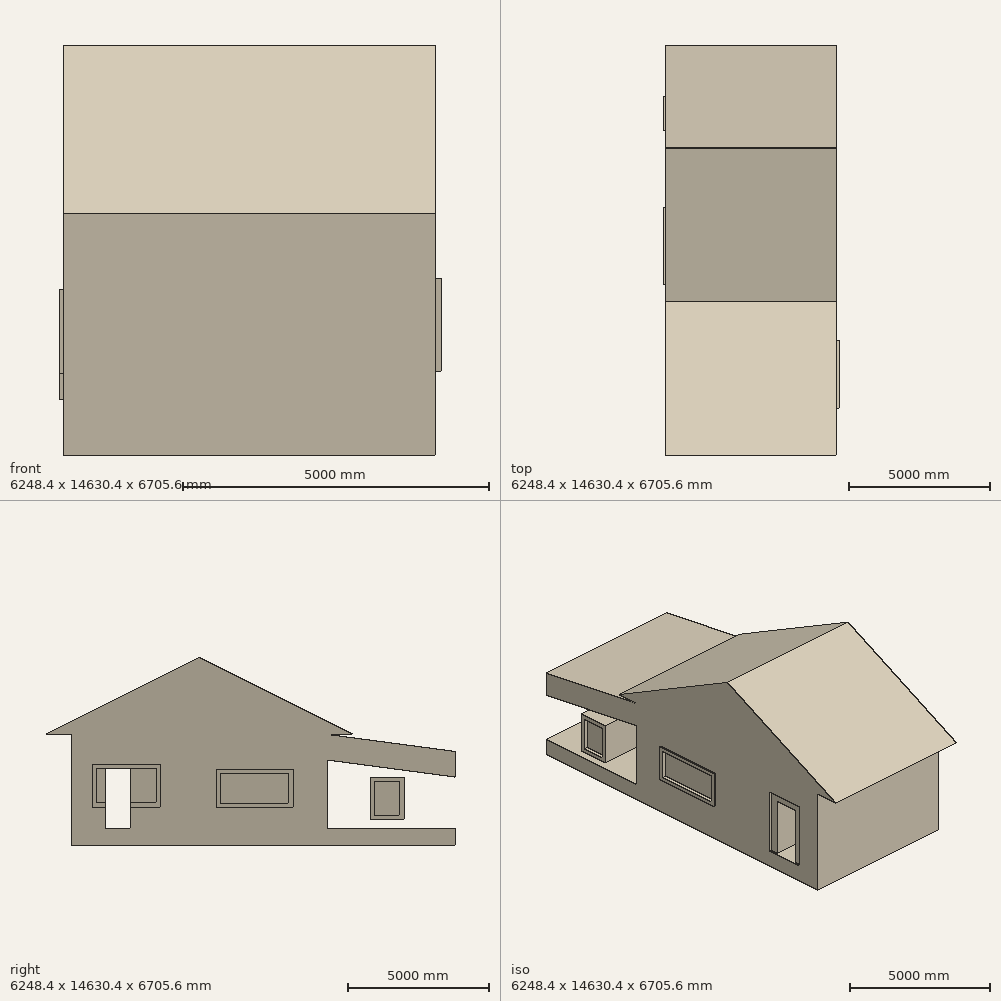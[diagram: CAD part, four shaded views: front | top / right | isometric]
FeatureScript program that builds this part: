
annotation { "Feature Type Name" : "Feature", "Feature Type Description" : "" }
export const myFeature = defineFeature(function(context is Context, id is Id, definition is map)
    precondition{}
    {
        {
            var Q0;
            Q0=qCreatedBy(makeId("Right.planeOp"),FACE);
            var sketch = newSketch(context, id + "F0", { "sketchPlane" : qUnion([Q0])});
            skLineSegment(sketch, "E0", {"start": v(0, 0) * mm, "end": v(-4572, 0) * mm});
            skLineSegment(sketch, "E1", {"start": v(0, 0) * mm, "end": v(4572, 0) * mm});
            skLineSegment(sketch, "E2", {"start": v(0, 0) * mm, "end": v(0, 2286) * mm});
            skLineSegment(sketch, "E3", {"start": v(0, 2286) * mm, "end": v(-4572, 0) * mm});
            skLineSegment(sketch, "E4", {"start": v(0, 2286) * mm, "end": v(4572, 0) * mm});
            skLineSegment(sketch, "E5", {"start": v(0, 2286) * mm, "end": v(0, 2743.2) * mm});
            skLineSegment(sketch, "E6", {"start": v(-4572, 0) * mm, "end": v(-5486.4, 0) * mm});
            skLineSegment(sketch, "E7", {"start": v(0, 2743.2) * mm, "end": v(-5486.4, 0) * mm});
            skLineSegment(sketch, "E8", {"start": v(4572, 0) * mm, "end": v(5486.4, 0) * mm});
            skLineSegment(sketch, "E9", {"start": v(0, 2743.2) * mm, "end": v(5486.4, 0) * mm});
            skLineSegment(sketch, "E10", {"start": v(-4572, 0) * mm, "end": v(-4572, -3352.8) * mm});
            skLineSegment(sketch, "E11", {"start": v(4572, 0) * mm, "end": v(4572, -3352.8) * mm});
            skLineSegment(sketch, "E12", {"start": v(-4572, -3352.8) * mm, "end": v(4572, -3352.8) * mm});
            skLineSegment(sketch, "E13", {"start": v(-4572, -3352.8) * mm, "end": v(-4572, -3962.4) * mm});
            skLineSegment(sketch, "E14", {"start": v(-4572, -3962.4) * mm, "end": v(4572, -3962.4) * mm});
            skLineSegment(sketch, "E15", {"start": v(4572, -3962.4) * mm, "end": v(4572, -3352.8) * mm});
            skLineSegment(sketch, "E16.bottom", {"start": v(609.6, -1252.99) * mm, "end": v(3352.8, -1252.99) * mm});
            skLineSegment(sketch, "E16.top", {"start": v(609.6, -2624.59) * mm, "end": v(3352.8, -2624.59) * mm});
            skLineSegment(sketch, "E16.left", {"start": v(609.6, -1252.99) * mm, "end": v(609.6, -2624.59) * mm});
            skLineSegment(sketch, "E16.right", {"start": v(3352.8, -1252.99) * mm, "end": v(3352.8, -2624.59) * mm});
            skLineSegment(sketch, "E17.0", {"start": v(762, -1405.39) * mm, "end": v(762, -2472.19) * mm});
            skLineSegment(sketch, "E17.1", {"start": v(762, -1405.39) * mm, "end": v(3200.4, -1405.39) * mm});
            skLineSegment(sketch, "E17.2", {"start": v(3200.4, -1405.39) * mm, "end": v(3200.4, -2472.19) * mm});
            skLineSegment(sketch, "E17.3", {"start": v(762, -2472.19) * mm, "end": v(3200.4, -2472.19) * mm});
            skLineSegment(sketch, "E18.top", {"start": v(-3358.31, -3352.8) * mm, "end": v(-1224.71, -3352.8) * mm});
            skLineSegment(sketch, "E19.bottom", {"start": v(-2438.4, -3352.8) * mm, "end": v(-3352.8, -3352.8) * mm});
            skLineSegment(sketch, "E19.top", {"start": v(-2438.4, -1219.2) * mm, "end": v(-3352.8, -1219.2) * mm});
            skLineSegment(sketch, "E19.left", {"start": v(-2438.4, -3352.8) * mm, "end": v(-2438.4, -1219.2) * mm});
            skLineSegment(sketch, "E19.right", {"start": v(-3352.8, -3352.8) * mm, "end": v(-3352.8, -1219.2) * mm});
            skLineSegment(sketch, "E20.0", {"start": v(-2133.6, -3352.8) * mm, "end": v(-2133.6, -914.4) * mm});
            skLineSegment(sketch, "E20.1", {"start": v(-2133.6, -914.4) * mm, "end": v(-3657.6, -914.4) * mm});
            skLineSegment(sketch, "E20.2", {"start": v(-3657.6, -3352.8) * mm, "end": v(-3657.6, -914.4) * mm});
            skLineSegment(sketch, "E21", {"start": v(4572, -3962.4) * mm, "end": v(9144, -3962.4) * mm});
            skLineSegment(sketch, "E22", {"start": v(4572, -3352.8) * mm, "end": v(9144, -3352.8) * mm});
            skLineSegment(sketch, "E23", {"start": v(9144, -3962.4) * mm, "end": v(9144, -3352.8) * mm});
            skLineSegment(sketch, "E24", {"start": v(9144, -3352.8) * mm, "end": v(9144, -609.6) * mm});
            skLineSegment(sketch, "E25", {"start": v(4572, 0) * mm, "end": v(4572, -914.4) * mm});
            skLineSegment(sketch, "E26", {"start": v(4572, 0) * mm, "end": v(9144, -609.6) * mm});
            skLineSegment(sketch, "E27", {"start": v(4572, -914.4) * mm, "end": v(9144, -1524) * mm});
            skLineSegment(sketch, "E28.bottom", {"start": v(6096, -1524) * mm, "end": v(7315.2, -1524) * mm});
            skLineSegment(sketch, "E28.top", {"start": v(6096, -3048) * mm, "end": v(7315.2, -3048) * mm});
            skLineSegment(sketch, "E28.left", {"start": v(6096, -1524) * mm, "end": v(6096, -3048) * mm});
            skLineSegment(sketch, "E28.right", {"start": v(7315.2, -1524) * mm, "end": v(7315.2, -3048) * mm});
            skLineSegment(sketch, "E29.0", {"start": v(6248.4, -1676.4) * mm, "end": v(6248.4, -2895.6) * mm});
            skLineSegment(sketch, "E29.1", {"start": v(6248.4, -1676.4) * mm, "end": v(7162.8, -1676.4) * mm});
            skLineSegment(sketch, "E29.2", {"start": v(7162.8, -1676.4) * mm, "end": v(7162.8, -2895.6) * mm});
            skLineSegment(sketch, "E29.3", {"start": v(6248.4, -2895.6) * mm, "end": v(7162.8, -2895.6) * mm});
            skText(sketch, "E30", { "text": "Michael", "fontName": "OpenSans-Regular.ttf"});
            skLineSegment(sketch, "E31", {"start": v(-3657.6, -3352.8) * mm, "end": v(-3352.8, -3352.8) * mm});
            skLineSegment(sketch, "E32", {"start": v(-2438.4, -3352.8) * mm, "end": v(-2133.6, -3352.8) * mm});
            const initialGuessF0  = {"E30": [-7.51989, 5.0648, 1, 0, 4.33686]};
            skSetInitialGuess(sketch, initialGuessF0);
            skSolve(sketch);
        }
        {
            var Q0;
            Q0=makeQuery(id+"F0.imprint","IMPRINT",FACE,{"disambiguationData":[TD([[makeQuery(id+"F0.imprint","IMPRINT",EDGE,{"derivedFrom":sQuery(id+"F0.wireOp",EDGE,"E0")}),1.0]])]});
            var Q1;
            Q1=makeQuery(id+"F0.imprint","IMPRINT",FACE,{"disambiguationData":[TD([[makeQuery(id+"F0.imprint","IMPRINT",EDGE,{"derivedFrom":sQuery(id+"F0.wireOp",EDGE,"E1")}),1.0]])]});
            var Q2;
            Q2=makeQuery(id+"F0.imprint","IMPRINT",FACE,{"disambiguationData":[TD([[makeQuery(id+"F0.imprint","IMPRINT",EDGE,{"derivedFrom":sQuery(id+"F0.wireOp",EDGE,"E0")}),-1.0]])]});
            var Q3;
            Q3=makeQuery(id+"F0.imprint","IMPRINT",FACE,{"disambiguationData":[TD([[makeQuery(id+"F0.imprint","IMPRINT",EDGE,{"derivedFrom":sQuery(id+"F0.wireOp",EDGE,"E11")}),1.0]])]});
            var Q4;
            Q4=makeQuery(id+"F0.imprint","IMPRINT",FACE,{"disambiguationData":[TD([[makeQuery(id+"F0.imprint","IMPRINT",EDGE,{"derivedFrom":sQuery(id+"F0.wireOp",EDGE,"E25")}),1.0]])]});
            var Q5;
            Q5=makeQuery(id+"F0.imprint","IMPRINT",FACE,{"disambiguationData":[TD([[makeQuery(id+"F0.imprint","IMPRINT",EDGE,{"derivedFrom":sQuery(id+"F0.wireOp",EDGE,"E15")}),-1.0]])]});
            var Q6;
            {var subQ0=sQuery(id+"F0.wireOp",EDGE,"E13");Q6=makeQuery(id+"F0.imprint","IMPRINT",FACE,{"disambiguationData":[TD([[makeQuery(id+"F0.imprint","IMPRINT",EDGE,{"derivedFrom":subQ0}),1.0]])]});}
            var Q7;
            Q7=makeQuery(id+"F0.imprint","IMPRINT",FACE,{"disambiguationData":[TD([[makeQuery(id+"F0.imprint","IMPRINT",EDGE,{"derivedFrom":sQuery(id+"F0.wireOp",EDGE,"E3")}),-1.0]])]});
            var Q8;
            Q8=makeQuery(id+"F0.imprint","IMPRINT",FACE,{"disambiguationData":[TD([[makeQuery(id+"F0.imprint","IMPRINT",EDGE,{"derivedFrom":sQuery(id+"F0.wireOp",EDGE,"E4")}),1.0]])]});
            extrude(context, id + "F1", {"entities" : qUnion([Q0, Q1, Q2, Q3, Q4, Q5, Q6, Q7, Q8]), "oppositeDirection" : true, "depth" : 6096 * mm, "offsetDistance" : 30.48 * mm});
        }
        {
            var Q0;
            Q0=makeQuery(id+"F0.imprint","IMPRINT",FACE,{"disambiguationData":[TD([[makeQuery(id+"F0.imprint","IMPRINT",EDGE,{"derivedFrom":sQuery(id+"F0.wireOp",EDGE,"E19.top")}),-1.0]])]});
            var Q1;
            Q1=makeQuery(id+"F0.imprint","IMPRINT",FACE,{"disambiguationData":[TD([[makeQuery(id+"F0.imprint","IMPRINT",EDGE,{"derivedFrom":sQuery(id+"F0.wireOp",EDGE,"E19.bottom")}),-1.0]])]});
            var Q2;
            Q2=makeQuery(id+"F0.imprint","IMPRINT",FACE,{"disambiguationData":[TD([[makeQuery(id+"F0.imprint","IMPRINT",EDGE,{"derivedFrom":sQuery(id+"F0.wireOp",EDGE,"E17.0")}),1.0]])]});
            var Q3;
            Q3=makeQuery(id+"F0.imprint","IMPRINT",FACE,{"disambiguationData":[TD([[makeQuery(id+"F0.imprint","IMPRINT",EDGE,{"derivedFrom":sQuery(id+"F0.wireOp",EDGE,"E29.0")}),1.0]])]});
            extrude(context, id + "F2", {"entities" : qUnion([Q0, Q1, Q2, Q3]), "operationType" : NewBodyOperationType.ADD, "oppositeDirection" : true, "depth" : 6004.56 * mm, "offsetDistance" : 30.48 * mm});
        }
        {
            var Q0;
            Q0=makeQuery(id+"F0.imprint","IMPRINT",FACE,{"disambiguationData":[TD([[makeQuery(id+"F0.imprint","IMPRINT",EDGE,{"derivedFrom":sQuery(id+"F0.wireOp",EDGE,"E16.bottom")}),-1.0]])]});
            var Q1;
            Q1=makeQuery(id+"F0.imprint","IMPRINT",FACE,{"disambiguationData":[TD([[makeQuery(id+"F0.imprint","IMPRINT",EDGE,{"derivedFrom":sQuery(id+"F0.wireOp",EDGE,"E28.bottom")}),-1.0]])]});
            extrude(context, id + "F3", {"entities" : qUnion([Q0, Q1]), "oppositeDirection" : true, "depth" : 6156.96 * mm, "offsetDistance" : 30.48 * mm});
        }
        {
            var Q0;
            {var subQ0=sQuery(id+"F0.wireOp",EDGE,"E32");var subQ1=sQuery(id+"F0.wireOp",EDGE,"E31");var subQ2=sQuery(id+"F0.wireOp",EDGE,"E20.2");var subQ3=sQuery(id+"F0.wireOp",EDGE,"E20.1");var subQ4=sQuery(id+"F0.wireOp",EDGE,"E20.0");var subQ5=sQuery(id+"F0.wireOp",EDGE,"E19.bottom");Q0=makeQuery(id+"F2.boolean.opBoolean","MERGE",FACE,{"derivedFrom":[makeQuery(id+"F1.opExtrude","CAP_FACE",FACE,{"disambiguationData":[OSD([sQuery(id+"F0.wireOp",EDGE,"E6"),sQuery(id+"F0.wireOp",EDGE,"E7"),sQuery(id+"F0.wireOp",EDGE,"E8"),sQuery(id+"F0.wireOp",EDGE,"E9"),sQuery(id+"F0.wireOp",EDGE,"E10"),sQuery(id+"F0.wireOp",EDGE,"E13"),sQuery(id+"F0.wireOp",EDGE,"E14"),sQuery(id+"F0.wireOp",EDGE,"E16.bottom"),sQuery(id+"F0.wireOp",EDGE,"E16.top"),sQuery(id+"F0.wireOp",EDGE,"E16.left"),sQuery(id+"F0.wireOp",EDGE,"E16.right"),subQ5,subQ4,subQ3,subQ2,sQuery(id+"F0.wireOp",EDGE,"E21"),sQuery(id+"F0.wireOp",EDGE,"E23"),sQuery(id+"F0.wireOp",EDGE,"E24"),sQuery(id+"F0.wireOp",EDGE,"E26"),sQuery(id+"F0.wireOp",EDGE,"E28.bottom"),sQuery(id+"F0.wireOp",EDGE,"E28.top"),sQuery(id+"F0.wireOp",EDGE,"E28.left"),sQuery(id+"F0.wireOp",EDGE,"E28.right"),subQ1,subQ0])],"isStart":true}),makeQuery(id+"F2.opExtrude","CAP_FACE",FACE,{"disambiguationData":[OSD([subQ5,subQ4,subQ3,subQ2,subQ1,subQ0])],"isStart":true})]});}
            var sketch = newSketch(context, id + "F4", { "sketchPlane" : qUnion([Q0])});
            skLineSegment(sketch, "E33.bottom", {"start": v(-3810, -1066.8) * mm, "end": v(-1371.6, -1066.8) * mm});
            skLineSegment(sketch, "E33.top", {"start": v(-3810, -2590.8) * mm, "end": v(-1371.6, -2590.8) * mm});
            skLineSegment(sketch, "E33.left", {"start": v(-3810, -1066.8) * mm, "end": v(-3810, -2590.8) * mm});
            skLineSegment(sketch, "E33.right", {"start": v(-1371.6, -1066.8) * mm, "end": v(-1371.6, -2590.8) * mm});
            skLineSegment(sketch, "E34.0", {"start": v(-3657.6, -1219.2) * mm, "end": v(-1524, -1219.2) * mm});
            skLineSegment(sketch, "E34.1", {"start": v(-3657.6, -1219.2) * mm, "end": v(-3657.6, -2438.4) * mm});
            skLineSegment(sketch, "E34.2", {"start": v(-3657.6, -2438.4) * mm, "end": v(-1524, -2438.4) * mm});
            skLineSegment(sketch, "E34.3", {"start": v(-1524, -1219.2) * mm, "end": v(-1524, -2438.4) * mm});
            skSolve(sketch);
        }
        {
            var Q0;
            Q0=makeQuery(id+"F4.imprint","IMPRINT",FACE,{"disambiguationData":[TD([[makeQuery(id+"F4.imprint","IMPRINT",EDGE,{"derivedFrom":sQuery(id+"F4.wireOp",EDGE,"E33.bottom")}),-1.0]])]});
            extrude(context, id + "F5", {"entities" : qUnion([Q0]), "operationType" : NewBodyOperationType.ADD, "depth" : 91.44 * mm, "offsetDistance" : 30.48 * mm});
        }
    });
